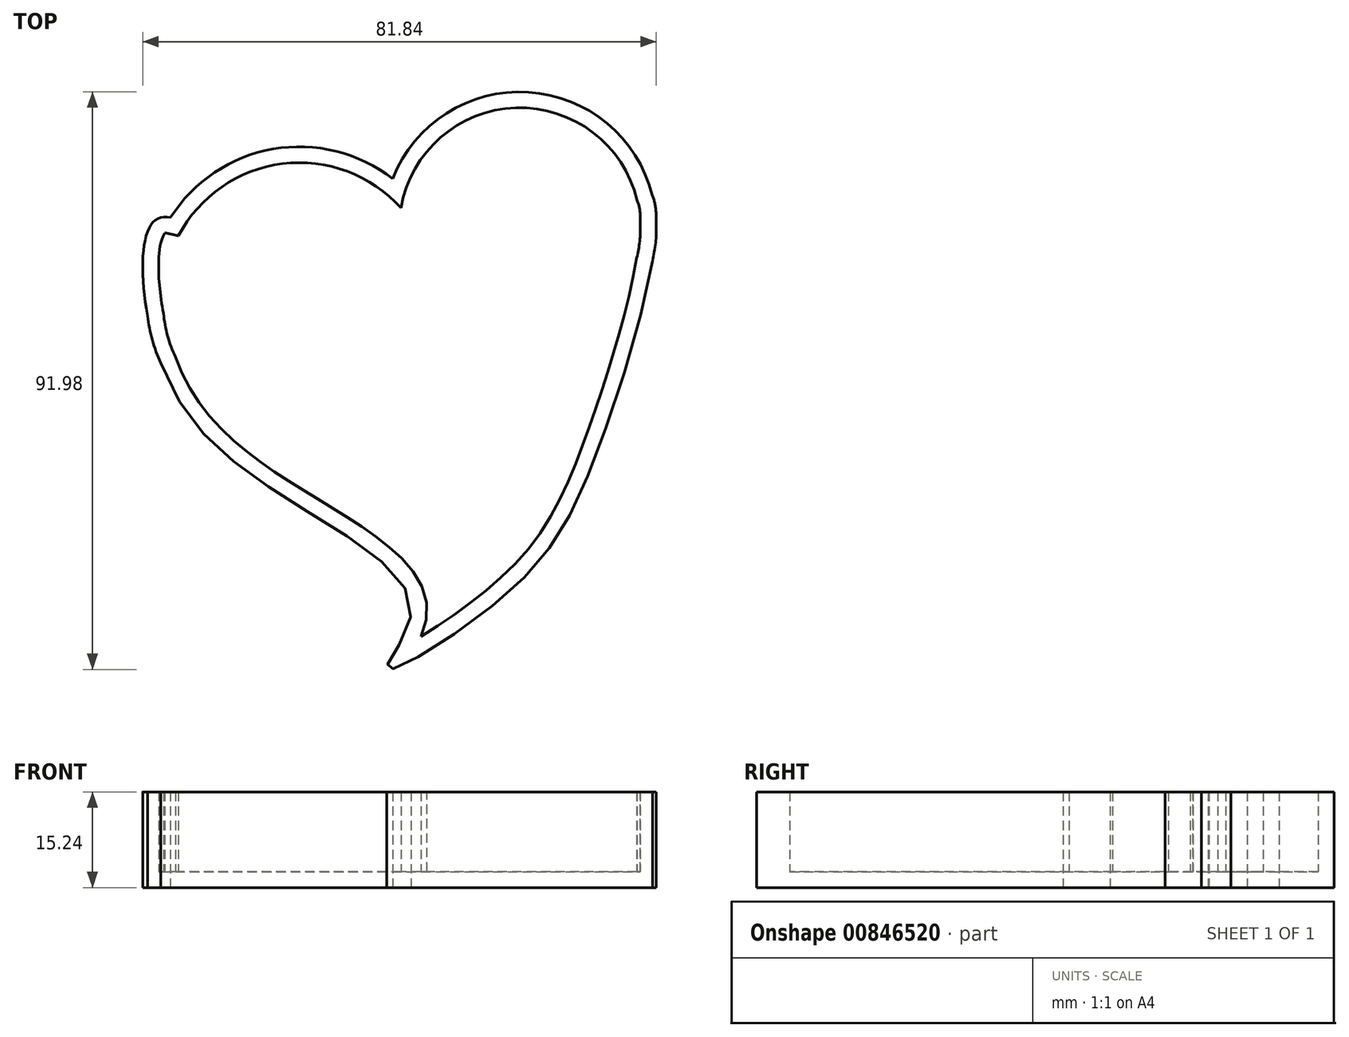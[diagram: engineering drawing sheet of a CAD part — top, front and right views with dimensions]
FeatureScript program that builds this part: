
annotation { "Feature Type Name" : "Feature", "Feature Type Description" : "" }
export const myFeature = defineFeature(function(context is Context, id is Id, definition is map)
    precondition{}
    {
        {
            var Q0;
            Q0=qCreatedBy(makeId("Top.planeOp"),FACE);
            var sketch = newSketch(context, id + "F0", { "sketchPlane" : qUnion([Q0])});
            skCircle(sketch, "E0", {"center": v(-17.75, 10.14) * mm, "radius": 24.3 * mm});
            skPoint(sketch, "E0.first.point", {"position": v(-31, 30.52) * mm});
            skPoint(sketch, "E0.second.point", {"position": v(4.63, 0.63) * mm});
            skPoint(sketch, "E0.third.point", {"position": v(0, 26.75) * mm});
            skCircle(sketch, "E1", {"center": v(17.38, 21.44) * mm, "radius": 21.75 * mm});
            skPoint(sketch, "E1.first.point", {"position": v(-3.7, 16.13) * mm});
            skPoint(sketch, "E1.second.point", {"position": v(38.47, 26.75) * mm});
            skPoint(sketch, "E1.third.point", {"position": v(21.02, 0) * mm});
            skFitSpline(sketch, "E2.trimOffspring", {"points": [v(-40.28, 23.03) * mm, v(-39.84, 0) * mm, v(-19.56, -21.72) * mm, v(0.05, -39.4) * mm, v(-3.8, -48.64) * mm, v(14.15, -37.74) * mm, v(30.24, -12.71) * mm, v(37.93, 27.6) * mm, v(17.66, 19.43) * mm, v(-18.8, 12.27) * mm, v(-40.28, 23.03) * mm]});
            skPoint(sketch, "E3.3.internal.orphan", {"position": v(0, -39.42) * mm});
            skPoint(sketch, "E3.4.internal.orphan", {"position": v(-3.7, -48.62) * mm});
            skSolve(sketch);
        }
        {
            var Q0;
            Q0 = qSketchRegion(id + "F0", true);
            var Q1;
            {var subQ0=sQuery(id+"F0.wireOp",EDGE,"E1");var subQ1=sQuery(id+"F0.wireOp",EDGE,"E0");var subQ2=makeQuery(id+"F0.imprint","INTERSECT",VERTEX,{"disambiguationData":[OD(1.0)],"derivedFrom":[subQ1,subQ0]});Q1=makeQuery(id+"F0.imprint","IMPRINT",FACE,{"disambiguationData":[TD([[makeQuery(id+"F0.imprint","IMPRINT",EDGE,{"disambiguationData":[TD([[subQ2,-1.0]])],"derivedFrom":subQ1}),1.0]])]});}
            extrude(context, id + "F1", {"entities" : qUnion([Q0, Q1]), "depth" : 15.24 * mm, "offsetDistance" : 25.4 * mm});
        }
        {
            var Q0;
            Q0=makeQuery(id+"F1.opExtrude","CAP_FACE",FACE,{"disambiguationData":[OSD([sQuery(id+"F0.wireOp",EDGE,"E0"),sQuery(id+"F0.wireOp",EDGE,"E1"),sQuery(id+"F0.wireOp",EDGE,"E2.trimOffspring")])],"isStart":false});
            shell(context, id + "F2", {"entities" : qUnion([Q0]), "thickness" : 2.54 * mm});
        }
    });
